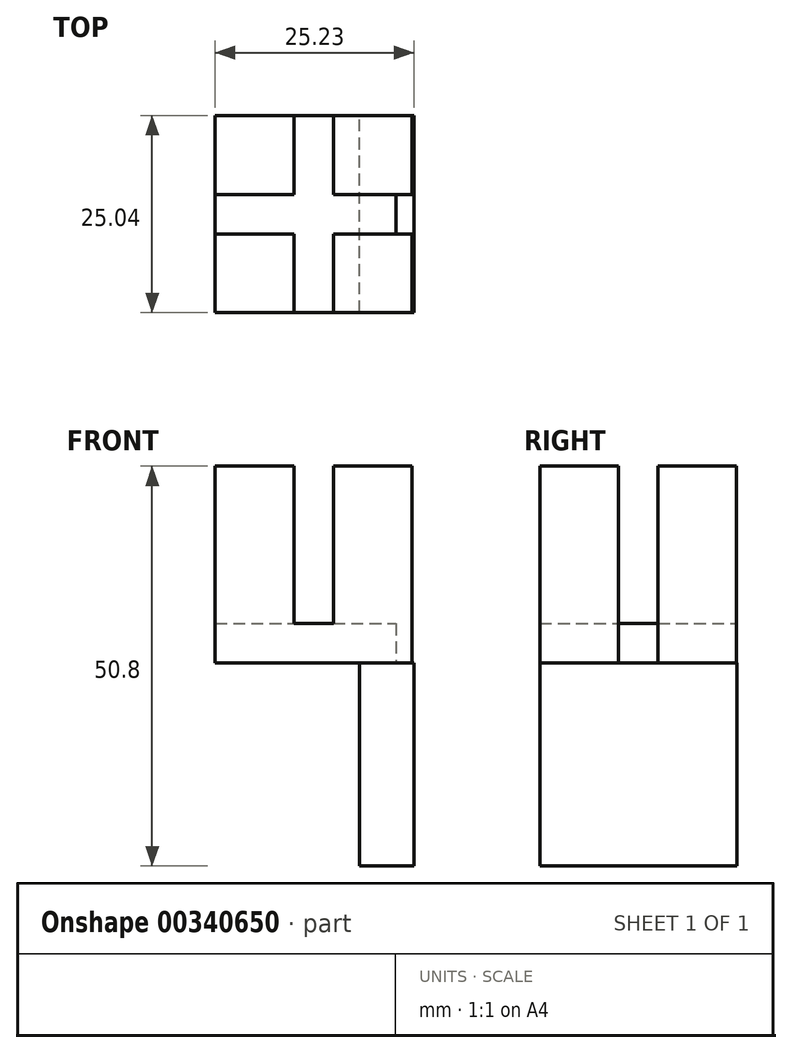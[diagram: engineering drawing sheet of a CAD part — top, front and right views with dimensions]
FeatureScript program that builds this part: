
annotation { "Feature Type Name" : "Feature", "Feature Type Description" : "" }
export const myFeature = defineFeature(function(context is Context, id is Id, definition is map)
    precondition{}
    {
        {
            var Q0;
            Q0=qCreatedBy(makeId("Top.planeOp"),FACE);
            var sketch = newSketch(context, id + "F0", { "sketchPlane" : qUnion([Q0])});
            skLineSegment(sketch, "E0.bottom", {"start": v(5, 5) * mm, "end": v(15, 5) * mm});
            skLineSegment(sketch, "E0.top", {"start": v(5, 15) * mm, "end": v(15, 15) * mm});
            skLineSegment(sketch, "E0.left", {"start": v(5, 5) * mm, "end": v(5, 15) * mm});
            skLineSegment(sketch, "E0.right", {"start": v(15, 5) * mm, "end": v(15, 15) * mm});
            skLineSegment(sketch, "E1.0.1.0", {"start": v(5, 30) * mm, "end": v(15, 30) * mm});
            skLineSegment(sketch, "E1.0.1.1", {"start": v(5, 20) * mm, "end": v(5, 30) * mm});
            skLineSegment(sketch, "E1.0.1.2", {"start": v(5, 20) * mm, "end": v(15, 20) * mm});
            skLineSegment(sketch, "E1.0.1.3", {"start": v(15, 20) * mm, "end": v(15, 30) * mm});
            skLineSegment(sketch, "E1.1.0.0", {"start": v(20, 15) * mm, "end": v(30, 15) * mm});
            skLineSegment(sketch, "E1.1.0.1", {"start": v(20, 5) * mm, "end": v(20, 15) * mm});
            skLineSegment(sketch, "E1.1.0.2", {"start": v(20, 5) * mm, "end": v(30, 5) * mm});
            skLineSegment(sketch, "E1.1.0.3", {"start": v(30, 5) * mm, "end": v(30, 15) * mm});
            skLineSegment(sketch, "E1.1.1.0", {"start": v(20, 30) * mm, "end": v(30, 30) * mm});
            skLineSegment(sketch, "E1.1.1.1", {"start": v(20, 20) * mm, "end": v(20, 30) * mm});
            skLineSegment(sketch, "E1.1.1.2", {"start": v(20, 20) * mm, "end": v(30, 20) * mm});
            skLineSegment(sketch, "E1.1.1.3", {"start": v(30, 20) * mm, "end": v(30, 30) * mm});
            skLineSegment(sketch, "E1.direction1", {"start": v(5, 15) * mm, "end": v(20, 15) * mm, "construction": true});
            skLineSegment(sketch, "E1.direction2", {"start": v(5, 15) * mm, "end": v(5, 30) * mm, "construction": true});
            skSolve(sketch);
        }
        {
            var Q0;
            Q0=makeQuery(id+"F0.imprint","IMPRINT",FACE,{"disambiguationData":[TD([[makeQuery(id+"F0.imprint","IMPRINT",EDGE,{"derivedFrom":sQuery(id+"F0.wireOp",EDGE,"E1.0.1.0")}),-1.0]])]});
            var Q1;
            Q1=makeQuery(id+"F0.imprint","IMPRINT",FACE,{"disambiguationData":[TD([[makeQuery(id+"F0.imprint","IMPRINT",EDGE,{"derivedFrom":sQuery(id+"F0.wireOp",EDGE,"E1.1.1.0")}),-1.0]])]});
            var Q2;
            Q2=makeQuery(id+"F0.imprint","IMPRINT",FACE,{"disambiguationData":[TD([[makeQuery(id+"F0.imprint","IMPRINT",EDGE,{"derivedFrom":sQuery(id+"F0.wireOp",EDGE,"E1.1.0.0")}),-1.0]])]});
            var Q3;
            Q3=makeQuery(id+"F0.imprint","IMPRINT",FACE,{"disambiguationData":[TD([[makeQuery(id+"F0.imprint","IMPRINT",EDGE,{"derivedFrom":sQuery(id+"F0.wireOp",EDGE,"E0.bottom")}),1.0]])]});
            extrude(context, id + "F1", {"entities" : qUnion([Q0, Q1, Q2, Q3]), "depth" : 25 * mm});
        }
        {
            var Q0;
            Q0=qCreatedBy(makeId("Top.planeOp"),FACE);
            var sketch = newSketch(context, id + "F2", { "sketchPlane" : qUnion([Q0])});
            skLineSegment(sketch, "E2.bottom", {"start": v(5, 30) * mm, "end": v(27.99, 30) * mm});
            skLineSegment(sketch, "E2.top", {"start": v(5, 5) * mm, "end": v(27.99, 5) * mm});
            skLineSegment(sketch, "E2.left", {"start": v(5, 30) * mm, "end": v(5, 5) * mm});
            skLineSegment(sketch, "E2.right", {"start": v(27.99, 30) * mm, "end": v(27.99, 5) * mm});
            skSolve(sketch);
        }
        {
            var Q0;
            Q0 = qSketchRegion(id + "F2", true);
            extrude(context, id + "F3", {"entities" : qUnion([Q0]), "operationType" : NewBodyOperationType.ADD, "depth" : 5 * mm});
        }
        {
            var Q0;
            Q0=qCreatedBy(makeId("Top.planeOp"),FACE);
            var sketch = newSketch(context, id + "F4", { "sketchPlane" : qUnion([Q0])});
            skLineSegment(sketch, "E3.bottom", {"start": v(23.33, 5.04) * mm, "end": v(30.23, 5.04) * mm});
            skLineSegment(sketch, "E3.top", {"start": v(23.33, 30.04) * mm, "end": v(30.23, 30.04) * mm});
            skLineSegment(sketch, "E3.left", {"start": v(23.33, 5.04) * mm, "end": v(23.33, 30.04) * mm});
            skLineSegment(sketch, "E3.right", {"start": v(30.23, 5.04) * mm, "end": v(30.23, 30.04) * mm});
            skSolve(sketch);
        }
        {
            var Q0;
            Q0=makeQuery(id+"F4.imprint","IMPRINT",FACE,{"disambiguationData":[TD([[makeQuery(id+"F4.imprint","IMPRINT",EDGE,{"derivedFrom":sQuery(id+"F4.wireOp",EDGE,"E3.bottom")}),1.0]])]});
            extrude(context, id + "F5", {"entities" : qUnion([Q0]), "operationType" : NewBodyOperationType.ADD, "oppositeDirection" : true, "depth" : 25.8 * mm});
        }
    });
